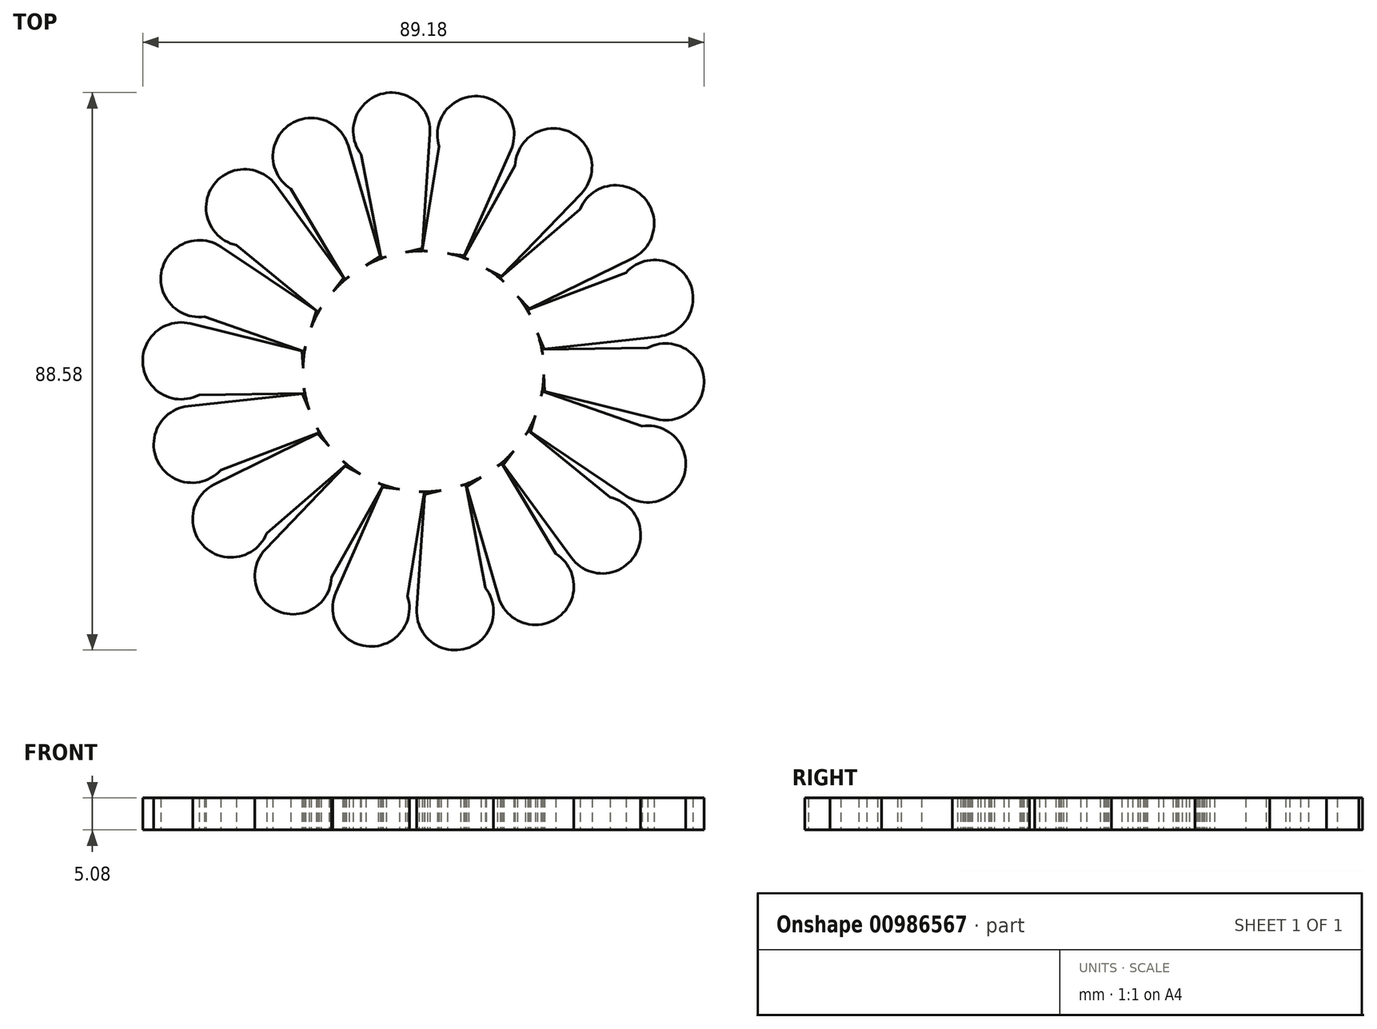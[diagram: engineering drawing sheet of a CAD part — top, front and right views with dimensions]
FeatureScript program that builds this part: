
annotation { "Feature Type Name" : "Feature", "Feature Type Description" : "" }
export const myFeature = defineFeature(function(context is Context, id is Id, definition is map)
    precondition{}
    {
        {
            var Q0;
            Q0=qCreatedBy(makeId("Top.planeOp"),FACE);
            var sketch = newSketch(context, id + "F0", { "sketchPlane" : qUnion([Q0])});
            skCircle(sketch, "E0", {"center": v(0, 0) * mm, "radius": 19.13 * mm});
            skSolve(sketch);
        }
        {
            var Q0;
            Q0=qCreatedBy(makeId("Top.planeOp"),FACE);
            var sketch = newSketch(context, id + "F1", { "sketchPlane" : qUnion([Q0])});
            skLineSegment(sketch, "E1", {"start": v(16.84, 9.93) * mm, "end": v(33.24, 17.99) * mm});
            skArc(sketch, "E2", {"start": v(33.24, 17.99) * mm, "mid": v(34.7, 27.93) * mm, "end": v(24.9, 25.76) * mm});
            skLineSegment(sketch, "E3", {"start": v(24.9, 25.76) * mm, "end": v(12.23, 14.82) * mm});
            skLineSegment(sketch, "E4", {"start": v(12.23, 14.82) * mm, "end": v(16.84, 9.93) * mm});
            skLineSegment(sketch, "E5.1.0", {"start": v(16.56, 9.74) * mm, "end": v(19.22, 3.57) * mm});
            skLineSegment(sketch, "E5.1.1", {"start": v(32.2, 15.7) * mm, "end": v(16.56, 9.74) * mm});
            skLineSegment(sketch, "E5.1.2", {"start": v(19.22, 3.57) * mm, "end": v(37.39, 5.53) * mm});
            skArc(sketch, "E5.1.3", {"start": v(37.39, 5.53) * mm, "mid": v(42.17, 14.38) * mm, "end": v(32.2, 15.7) * mm});
            skLineSegment(sketch, "E5.2.0", {"start": v(18.9, 3.5) * mm, "end": v(19.28, -3.22) * mm});
            skLineSegment(sketch, "E5.2.1", {"start": v(35.63, 3.73) * mm, "end": v(18.9, 3.5) * mm});
            skLineSegment(sketch, "E5.2.2", {"start": v(19.28, -3.22) * mm, "end": v(37.03, -7.59) * mm});
            skArc(sketch, "E5.2.3", {"start": v(37.03, -7.59) * mm, "mid": v(44.54, -0.91) * mm, "end": v(35.63, 3.73) * mm});
            skLineSegment(sketch, "E5.3.0", {"start": v(18.95, -3.18) * mm, "end": v(17.02, -9.62) * mm});
            skLineSegment(sketch, "E5.3.1", {"start": v(34.76, -8.68) * mm, "end": v(18.95, -3.18) * mm});
            skLineSegment(sketch, "E5.3.2", {"start": v(17.02, -9.62) * mm, "end": v(32.2, -19.8) * mm});
            skArc(sketch, "E5.3.3", {"start": v(32.2, -19.8) * mm, "mid": v(41.54, -16.1) * mm, "end": v(34.76, -8.68) * mm});
            skLineSegment(sketch, "E5.4.0", {"start": v(16.72, -9.47) * mm, "end": v(12.7, -14.86) * mm});
            skLineSegment(sketch, "E5.4.1", {"start": v(29.7, -20.04) * mm, "end": v(16.72, -9.47) * mm});
            skLineSegment(sketch, "E5.4.2", {"start": v(12.7, -14.86) * mm, "end": v(23.49, -29.61) * mm});
            skArc(sketch, "E5.4.3", {"start": v(23.49, -29.61) * mm, "mid": v(33.53, -29.33) * mm, "end": v(29.7, -20.04) * mm});
            skLineSegment(sketch, "E5.5.0", {"start": v(12.47, -14.62) * mm, "end": v(6.85, -18.3) * mm});
            skLineSegment(sketch, "E5.5.1", {"start": v(21.04, -28.99) * mm, "end": v(12.47, -14.62) * mm});
            skLineSegment(sketch, "E5.5.2", {"start": v(6.85, -18.3) * mm, "end": v(11.94, -35.86) * mm});
            skArc(sketch, "E5.5.3", {"start": v(11.94, -35.86) * mm, "mid": v(21.48, -39.03) * mm, "end": v(21.04, -28.99) * mm});
            skLineSegment(sketch, "E5.6.0", {"start": v(6.72, -18) * mm, "end": v(0.18, -19.55) * mm});
            skLineSegment(sketch, "E5.6.1", {"start": v(9.86, -34.44) * mm, "end": v(6.72, -18) * mm});
            skLineSegment(sketch, "E5.6.2", {"start": v(0.18, -19.55) * mm, "end": v(-1.04, -37.78) * mm});
            skArc(sketch, "E5.6.3", {"start": v(-1.04, -37.78) * mm, "mid": v(6.84, -44.03) * mm, "end": v(9.86, -34.44) * mm});
            skLineSegment(sketch, "E5.7.0", {"start": v(0.16, -19.22) * mm, "end": v(-6.52, -18.43) * mm});
            skLineSegment(sketch, "E5.7.1", {"start": v(-2.51, -35.73) * mm, "end": v(0.16, -19.22) * mm});
            skLineSegment(sketch, "E5.7.2", {"start": v(-6.52, -18.43) * mm, "end": v(-13.9, -35.15) * mm});
            skArc(sketch, "E5.7.3", {"start": v(-13.9, -35.15) * mm, "mid": v(-8.63, -43.7) * mm, "end": v(-2.51, -35.73) * mm});
            skLineSegment(sketch, "E5.8.0", {"start": v(-6.42, -18.11) * mm, "end": v(-12.43, -15.09) * mm});
            skLineSegment(sketch, "E5.8.1", {"start": v(-14.58, -32.72) * mm, "end": v(-6.42, -18.11) * mm});
            skLineSegment(sketch, "E5.8.2", {"start": v(-12.43, -15.09) * mm, "end": v(-25.08, -28.27) * mm});
            skArc(sketch, "E5.8.3", {"start": v(-25.08, -28.27) * mm, "mid": v(-23.06, -38.12) * mm, "end": v(-14.58, -32.72) * mm});
            skLineSegment(sketch, "E5.9.0", {"start": v(-12.23, -14.82) * mm, "end": v(-16.84, -9.93) * mm});
            skLineSegment(sketch, "E5.9.1", {"start": v(-24.9, -25.76) * mm, "end": v(-12.23, -14.82) * mm});
            skLineSegment(sketch, "E5.9.2", {"start": v(-16.84, -9.93) * mm, "end": v(-33.24, -17.99) * mm});
            skArc(sketch, "E5.9.3", {"start": v(-33.24, -17.99) * mm, "mid": v(-34.7, -27.93) * mm, "end": v(-24.9, -25.76) * mm});
            skLineSegment(sketch, "E5.10.0", {"start": v(-16.56, -9.74) * mm, "end": v(-19.22, -3.57) * mm});
            skLineSegment(sketch, "E5.10.1", {"start": v(-32.2, -15.7) * mm, "end": v(-16.56, -9.74) * mm});
            skLineSegment(sketch, "E5.10.2", {"start": v(-19.22, -3.57) * mm, "end": v(-37.39, -5.53) * mm});
            skArc(sketch, "E5.10.3", {"start": v(-37.39, -5.53) * mm, "mid": v(-42.17, -14.38) * mm, "end": v(-32.2, -15.7) * mm});
            skLineSegment(sketch, "E5.11.0", {"start": v(-18.9, -3.5) * mm, "end": v(-19.28, 3.22) * mm});
            skLineSegment(sketch, "E5.11.1", {"start": v(-35.63, -3.73) * mm, "end": v(-18.9, -3.5) * mm});
            skLineSegment(sketch, "E5.11.2", {"start": v(-19.28, 3.22) * mm, "end": v(-37.03, 7.59) * mm});
            skArc(sketch, "E5.11.3", {"start": v(-37.03, 7.59) * mm, "mid": v(-44.54, 0.91) * mm, "end": v(-35.63, -3.73) * mm});
            skLineSegment(sketch, "E5.12.0", {"start": v(-18.95, 3.18) * mm, "end": v(-17.02, 9.62) * mm});
            skLineSegment(sketch, "E5.12.1", {"start": v(-34.76, 8.68) * mm, "end": v(-18.95, 3.18) * mm});
            skLineSegment(sketch, "E5.12.2", {"start": v(-17.02, 9.62) * mm, "end": v(-32.2, 19.8) * mm});
            skArc(sketch, "E5.12.3", {"start": v(-32.2, 19.8) * mm, "mid": v(-41.54, 16.1) * mm, "end": v(-34.76, 8.68) * mm});
            skLineSegment(sketch, "E5.13.0", {"start": v(-16.72, 9.47) * mm, "end": v(-12.7, 14.86) * mm});
            skLineSegment(sketch, "E5.13.1", {"start": v(-29.7, 20.04) * mm, "end": v(-16.72, 9.47) * mm});
            skLineSegment(sketch, "E5.13.2", {"start": v(-12.7, 14.86) * mm, "end": v(-23.49, 29.61) * mm});
            skArc(sketch, "E5.13.3", {"start": v(-23.49, 29.61) * mm, "mid": v(-33.53, 29.33) * mm, "end": v(-29.7, 20.04) * mm});
            skLineSegment(sketch, "E5.14.0", {"start": v(-12.47, 14.62) * mm, "end": v(-6.85, 18.3) * mm});
            skLineSegment(sketch, "E5.14.1", {"start": v(-21.04, 28.99) * mm, "end": v(-12.47, 14.62) * mm});
            skLineSegment(sketch, "E5.14.2", {"start": v(-6.85, 18.3) * mm, "end": v(-11.94, 35.86) * mm});
            skArc(sketch, "E5.14.3", {"start": v(-11.94, 35.86) * mm, "mid": v(-21.48, 39.03) * mm, "end": v(-21.04, 28.99) * mm});
            skLineSegment(sketch, "E5.15.0", {"start": v(-6.72, 18) * mm, "end": v(-0.18, 19.55) * mm});
            skLineSegment(sketch, "E5.15.1", {"start": v(-9.86, 34.44) * mm, "end": v(-6.72, 18) * mm});
            skLineSegment(sketch, "E5.15.2", {"start": v(-0.18, 19.55) * mm, "end": v(1.04, 37.78) * mm});
            skArc(sketch, "E5.15.3", {"start": v(1.04, 37.78) * mm, "mid": v(-6.84, 44.03) * mm, "end": v(-9.86, 34.44) * mm});
            skLineSegment(sketch, "E5.16.0", {"start": v(-0.16, 19.22) * mm, "end": v(6.52, 18.43) * mm});
            skLineSegment(sketch, "E5.16.1", {"start": v(2.51, 35.73) * mm, "end": v(-0.16, 19.22) * mm});
            skLineSegment(sketch, "E5.16.2", {"start": v(6.52, 18.43) * mm, "end": v(13.9, 35.15) * mm});
            skArc(sketch, "E5.16.3", {"start": v(13.9, 35.15) * mm, "mid": v(8.63, 43.7) * mm, "end": v(2.51, 35.73) * mm});
            skLineSegment(sketch, "E5.17.0", {"start": v(6.42, 18.11) * mm, "end": v(12.43, 15.09) * mm});
            skLineSegment(sketch, "E5.17.1", {"start": v(14.58, 32.72) * mm, "end": v(6.42, 18.11) * mm});
            skLineSegment(sketch, "E5.17.2", {"start": v(12.43, 15.09) * mm, "end": v(25.08, 28.27) * mm});
            skArc(sketch, "E5.17.3", {"start": v(25.08, 28.27) * mm, "mid": v(23.06, 38.12) * mm, "end": v(14.58, 32.72) * mm});
            skPoint(sketch, "E5.center", {"position": v(0, 0) * mm});
            skLineSegment(sketch, "E5.anchor1", {"start": v(0, 0) * mm, "end": v(16.84, 9.93) * mm, "construction": true});
            skLineSegment(sketch, "E5.anchor2", {"start": v(0, 0) * mm, "end": v(12.43, 15.09) * mm, "construction": true});
            skSolve(sketch);
        }
        {
            var Q0;
            Q0=makeQuery(id+"F0.imprint","IMPRINT",FACE,{"disambiguationData":[TD([[makeQuery(id+"F0.imprint","IMPRINT",EDGE,{"derivedFrom":sQuery(id+"F0.wireOp",EDGE,"E0")}),1.0]])]});
            extrude(context, id + "F2", {"entities" : qUnion([Q0]), "depth" : 5.08 * mm, "offsetDistance" : 25.4 * mm});
        }
        {
            var Q0;
            Q0=makeQuery(id+"F1.imprint","IMPRINT",FACE,{"disambiguationData":[TD([[makeQuery(id+"F1.imprint","IMPRINT",EDGE,{"derivedFrom":sQuery(id+"F1.wireOp",EDGE,"E5.14.0")}),1.0]])]});
            var Q1;
            Q1=makeQuery(id+"F1.imprint","IMPRINT",FACE,{"disambiguationData":[TD([[makeQuery(id+"F1.imprint","IMPRINT",EDGE,{"derivedFrom":sQuery(id+"F1.wireOp",EDGE,"E5.15.0")}),1.0]])]});
            var Q2;
            Q2=makeQuery(id+"F1.imprint","IMPRINT",FACE,{"disambiguationData":[TD([[makeQuery(id+"F1.imprint","IMPRINT",EDGE,{"derivedFrom":sQuery(id+"F1.wireOp",EDGE,"E5.16.0")}),1.0]])]});
            var Q3;
            Q3=makeQuery(id+"F1.imprint","IMPRINT",FACE,{"disambiguationData":[TD([[makeQuery(id+"F1.imprint","IMPRINT",EDGE,{"derivedFrom":sQuery(id+"F1.wireOp",EDGE,"E5.17.0")}),1.0]])]});
            var Q4;
            Q4=makeQuery(id+"F1.imprint","IMPRINT",FACE,{"disambiguationData":[TD([[makeQuery(id+"F1.imprint","IMPRINT",EDGE,{"derivedFrom":sQuery(id+"F1.wireOp",EDGE,"E1")}),1.0]])]});
            var Q5;
            Q5=makeQuery(id+"F1.imprint","IMPRINT",FACE,{"disambiguationData":[TD([[makeQuery(id+"F1.imprint","IMPRINT",EDGE,{"derivedFrom":sQuery(id+"F1.wireOp",EDGE,"E5.1.0")}),1.0]])]});
            var Q6;
            Q6=makeQuery(id+"F1.imprint","IMPRINT",FACE,{"disambiguationData":[TD([[makeQuery(id+"F1.imprint","IMPRINT",EDGE,{"derivedFrom":sQuery(id+"F1.wireOp",EDGE,"E5.2.0")}),1.0]])]});
            var Q7;
            Q7=makeQuery(id+"F1.imprint","IMPRINT",FACE,{"disambiguationData":[TD([[makeQuery(id+"F1.imprint","IMPRINT",EDGE,{"derivedFrom":sQuery(id+"F1.wireOp",EDGE,"E5.3.0")}),1.0]])]});
            var Q8;
            Q8=makeQuery(id+"F1.imprint","IMPRINT",FACE,{"disambiguationData":[TD([[makeQuery(id+"F1.imprint","IMPRINT",EDGE,{"derivedFrom":sQuery(id+"F1.wireOp",EDGE,"E5.4.0")}),1.0]])]});
            var Q9;
            Q9=makeQuery(id+"F1.imprint","IMPRINT",FACE,{"disambiguationData":[TD([[makeQuery(id+"F1.imprint","IMPRINT",EDGE,{"derivedFrom":sQuery(id+"F1.wireOp",EDGE,"E5.5.0")}),1.0]])]});
            var Q10;
            Q10=makeQuery(id+"F1.imprint","IMPRINT",FACE,{"disambiguationData":[TD([[makeQuery(id+"F1.imprint","IMPRINT",EDGE,{"derivedFrom":sQuery(id+"F1.wireOp",EDGE,"E5.6.0")}),1.0]])]});
            var Q11;
            Q11=makeQuery(id+"F1.imprint","IMPRINT",FACE,{"disambiguationData":[TD([[makeQuery(id+"F1.imprint","IMPRINT",EDGE,{"derivedFrom":sQuery(id+"F1.wireOp",EDGE,"E5.7.0")}),1.0]])]});
            var Q12;
            Q12=makeQuery(id+"F1.imprint","IMPRINT",FACE,{"disambiguationData":[TD([[makeQuery(id+"F1.imprint","IMPRINT",EDGE,{"derivedFrom":sQuery(id+"F1.wireOp",EDGE,"E5.8.0")}),1.0]])]});
            var Q13;
            Q13=makeQuery(id+"F1.imprint","IMPRINT",FACE,{"disambiguationData":[TD([[makeQuery(id+"F1.imprint","IMPRINT",EDGE,{"derivedFrom":sQuery(id+"F1.wireOp",EDGE,"E5.9.0")}),1.0]])]});
            var Q14;
            Q14=makeQuery(id+"F1.imprint","IMPRINT",FACE,{"disambiguationData":[TD([[makeQuery(id+"F1.imprint","IMPRINT",EDGE,{"derivedFrom":sQuery(id+"F1.wireOp",EDGE,"E5.12.0")}),1.0]])]});
            var Q15;
            Q15=makeQuery(id+"F1.imprint","IMPRINT",FACE,{"disambiguationData":[TD([[makeQuery(id+"F1.imprint","IMPRINT",EDGE,{"derivedFrom":sQuery(id+"F1.wireOp",EDGE,"E5.13.0")}),1.0]])]});
            var Q16;
            Q16=makeQuery(id+"F1.imprint","IMPRINT",FACE,{"disambiguationData":[TD([[makeQuery(id+"F1.imprint","IMPRINT",EDGE,{"derivedFrom":sQuery(id+"F1.wireOp",EDGE,"E5.11.0")}),1.0]])]});
            var Q17;
            Q17=makeQuery(id+"F1.imprint","IMPRINT",FACE,{"disambiguationData":[TD([[makeQuery(id+"F1.imprint","IMPRINT",EDGE,{"derivedFrom":sQuery(id+"F1.wireOp",EDGE,"E5.10.0")}),1.0]])]});
            extrude(context, id + "F3", {"entities" : qUnion([Q0, Q1, Q2, Q3, Q4, Q5, Q6, Q7, Q8, Q9, Q10, Q11, Q12, Q13, Q14, Q15, Q16, Q17]), "operationType" : NewBodyOperationType.ADD, "depth" : 5.08 * mm, "offsetDistance" : 25.4 * mm});
        }
    });
